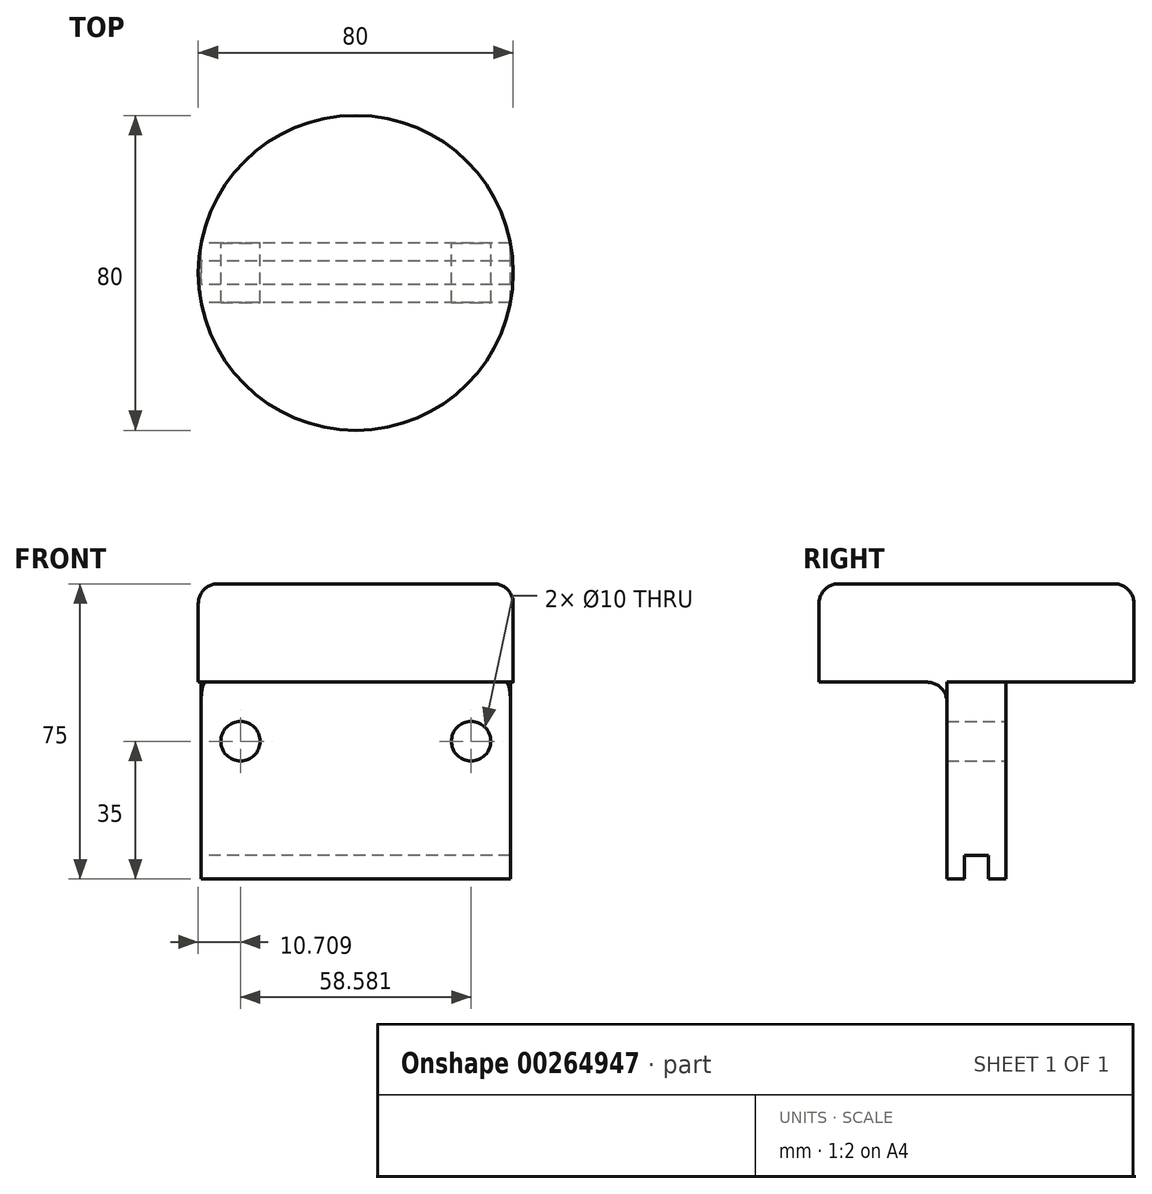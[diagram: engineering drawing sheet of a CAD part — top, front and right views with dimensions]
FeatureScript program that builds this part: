
annotation { "Feature Type Name" : "Feature", "Feature Type Description" : "" }
export const myFeature = defineFeature(function(context is Context, id is Id, definition is map)
    precondition{}
    {
        {
            var Q0;
            Q0=qCreatedBy(makeId("Top.planeOp"),FACE);
            var sketch = newSketch(context, id + "F0", { "sketchPlane" : qUnion([Q0])});
            skCircle(sketch, "E0", {"center": v(0, 0) * mm, "radius": 40 * mm});
            skSolve(sketch);
        }
        {
            var Q0;
            Q0 = qSketchRegion(id + "F0", true);
            extrude(context, id + "F1", {"entities" : qUnion([Q0]), "oppositeDirection" : true, "depth" : 25 * mm});
        }
        {
            var Q0;
            Q0=makeQuery(id+"F1.opExtrude","CAP_FACE",FACE,{"disambiguationData":[OSD([sQuery(id+"F0.wireOp",EDGE,"E0")])],"isStart":false});
            var sketch = newSketch(context, id + "F2", { "sketchPlane" : qUnion([Q0])});
            skLineSegment(sketch, "E1.bottom", {"start": v(39.3, 7.5) * mm, "end": v(-39.3, 7.5) * mm});
            skLineSegment(sketch, "E1.top", {"start": v(39.3, -7.5) * mm, "end": v(-39.3, -7.5) * mm});
            skLineSegment(sketch, "E1.left", {"start": v(39.3, 7.5) * mm, "end": v(39.3, -7.5) * mm});
            skLineSegment(sketch, "E1.right", {"start": v(-39.3, 7.5) * mm, "end": v(-39.3, -7.5) * mm});
            skPoint(sketch, "E1.middle", {"position": v(0, 0) * mm});
            skSolve(sketch);
        }
        {
            var Q0;
            Q0 = qSketchRegion(id + "F2", true);
            extrude(context, id + "F3", {"entities" : qUnion([Q0]), "operationType" : NewBodyOperationType.ADD, "depth" : 50 * mm});
        }
        {
            var Q0;
            Q0=makeQuery(id+"F3.opExtrude","SWEPT_FACE",FACE,{"disambiguationData":[OSD([sQuery(id+"F2.wireOp",EDGE,"E1.right")])]});
            var sketch = newSketch(context, id + "F4", { "sketchPlane" : qUnion([Q0])});
            skLineSegment(sketch, "E2.bottom", {"start": v(-3, -69) * mm, "end": v(3, -69) * mm});
            skLineSegment(sketch, "E2.top", {"start": v(3, -81) * mm, "end": v(-3, -81) * mm});
            skLineSegment(sketch, "E2.left", {"start": v(-3, -81) * mm, "end": v(-3, -69) * mm});
            skLineSegment(sketch, "E2.right", {"start": v(3, -81) * mm, "end": v(3, -69) * mm});
            skPoint(sketch, "E2.middle", {"position": v(0, -75) * mm});
            skSolve(sketch);
        }
        {
            var Q0;
            Q0 = qSketchRegion(id + "F4", true);
            extrude(context, id + "F5", {"entities" : qUnion([Q0]), "operationType" : NewBodyOperationType.REMOVE, "endBound" : BoundingType.THROUGH_ALL, "oppositeDirection" : true, "depth" : 88.2 * mm});
        }
        {
            var Q0;
            Q0=makeQuery(id+"F3.opExtrude","SWEPT_FACE",FACE,{"disambiguationData":[OSD([sQuery(id+"F2.wireOp",EDGE,"E1.top")])]});
            var sketch = newSketch(context, id + "F6", { "sketchPlane" : qUnion([Q0])});
            skCircle(sketch, "E3", {"center": v(-29.3, -40) * mm, "radius": 5 * mm});
            skCircle(sketch, "E4", {"center": v(29.3, -40) * mm, "radius": 5 * mm});
            skSolve(sketch);
        }
        {
            var Q0;
            Q0 = qSketchRegion(id + "F6", true);
            extrude(context, id + "F7", {"entities" : qUnion([Q0]), "operationType" : NewBodyOperationType.REMOVE, "oppositeDirection" : true, "depth" : 25 * mm});
        }
        {
            var Q0;
            Q0=makeQuery(id+"F1.opExtrude","CAP_EDGE",EDGE,{"disambiguationData":[OSD([sQuery(id+"F0.wireOp",EDGE,"E0")])],"isStart":true});
            var Q1;
            Q1=makeQuery(id+"F3.opExtrude","CAP_EDGE",EDGE,{"disambiguationData":[OSD([sQuery(id+"F2.wireOp",EDGE,"E1.bottom")])],"isStart":true});
            fillet(context, id + "F8", {"entities" : qUnion([Q0, Q1]), "radius" : 5 * mm, "tangentPropagation" : true, "allowEdgeOverflow" : false});
        }
    });
